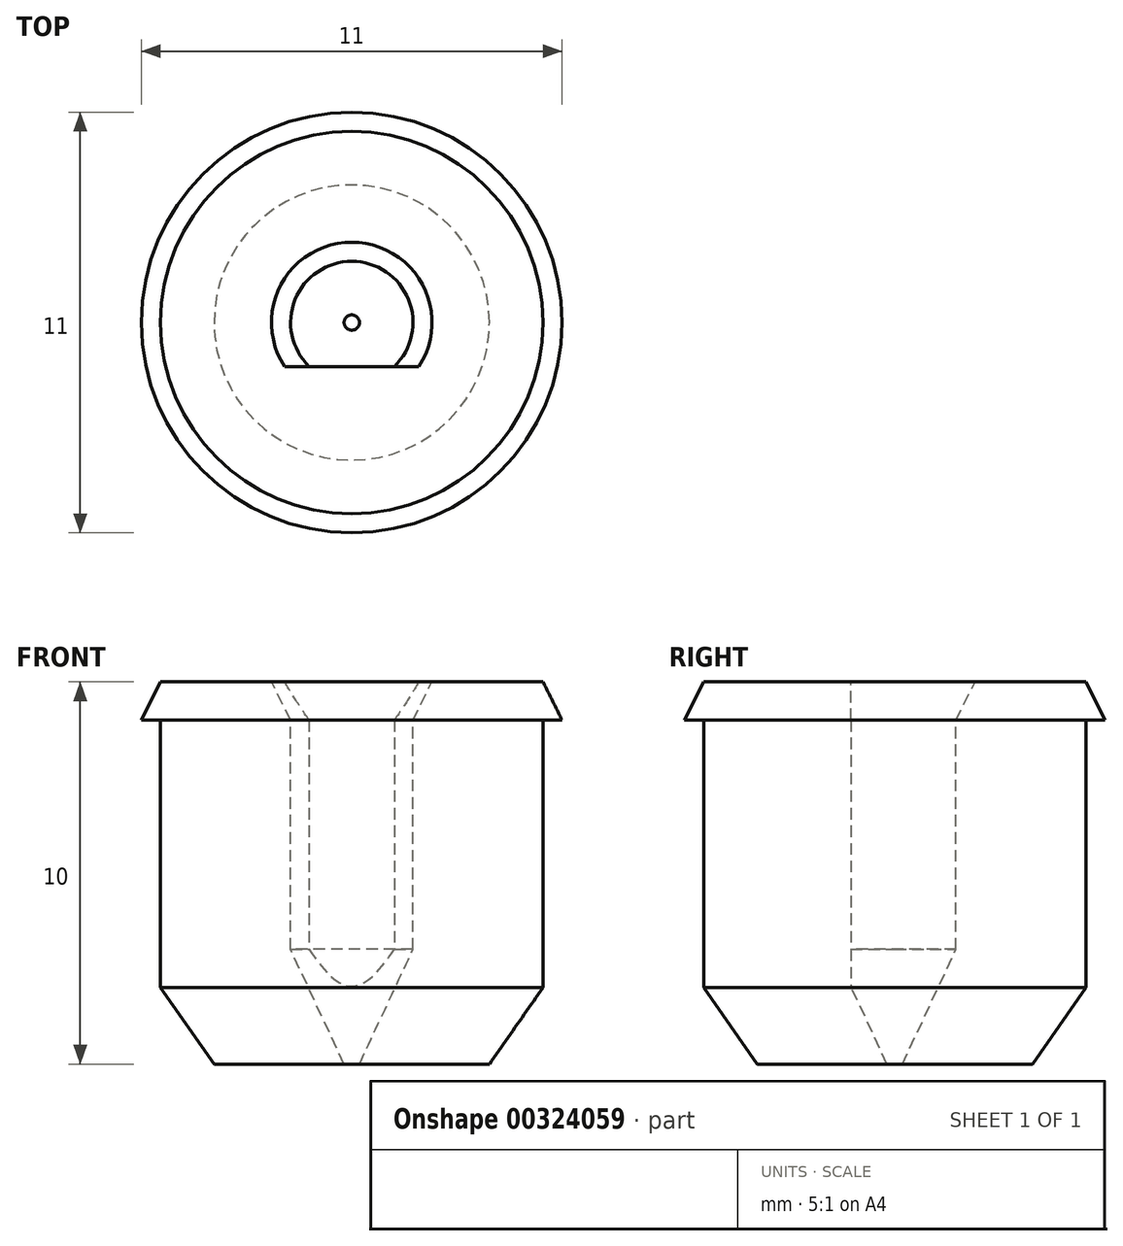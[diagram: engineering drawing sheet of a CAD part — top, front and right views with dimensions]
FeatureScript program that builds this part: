
annotation { "Feature Type Name" : "Feature", "Feature Type Description" : "" }
export const myFeature = defineFeature(function(context is Context, id is Id, definition is map)
    precondition{}
    {
        {
            var Q0;
            Q0=qCreatedBy(makeId("Front.planeOp"),FACE);
            var sketch = newSketch(context, id + "F0", { "sketchPlane" : qUnion([Q0])});
            skLineSegment(sketch, "E0", {"start": v(1.6, 10) * mm, "end": v(5.5, 10) * mm});
            skLineSegment(sketch, "E1", {"start": v(5.5, 10) * mm, "end": v(5.5, 9) * mm});
            skLineSegment(sketch, "E2", {"start": v(5.5, 9) * mm, "end": v(5, 9) * mm});
            skLineSegment(sketch, "E3", {"start": v(5, 9) * mm, "end": v(5, 2) * mm});
            skLineSegment(sketch, "E4", {"start": v(5, 2) * mm, "end": v(3.6, 0) * mm});
            skLineSegment(sketch, "E5", {"start": v(3.6, 0) * mm, "end": v(1.6, 0) * mm});
            skLineSegment(sketch, "E6", {"start": v(1.6, 0) * mm, "end": v(1.6, 10) * mm});
            skLineSegment(sketch, "E7", {"start": v(1.6, 3) * mm, "end": v(0.2, 0) * mm});
            skLineSegment(sketch, "E8", {"start": v(0, 10) * mm, "end": v(0, 0) * mm, "construction": true});
            skLineSegment(sketch, "E9", {"start": v(1.6, 0) * mm, "end": v(0.2, 0) * mm});
            skSolve(sketch);
        }
        {
            var Q0;
            Q0=makeQuery(id+"F0.imprint","IMPRINT",FACE,{"disambiguationData":[TD([[makeQuery(id+"F0.imprint","IMPRINT",EDGE,{"derivedFrom":sQuery(id+"F0.wireOp",EDGE,"E0")}),-1.0]])]});
            var Q1;
            {var subQ2=sQuery(id+"F0.wireOp",EDGE,"E7");Q1=makeQuery(id+"F0.imprint","IMPRINT",FACE,{"disambiguationData":[TD([[makeQuery(id+"F0.imprint","IMPRINT",EDGE,{"derivedFrom":subQ2}),1.0]])]});}
            var Q2;
            Q2=sQuery(id+"F0.wireOp",EDGE,"E8");
            revolve(context, id + "F1", {"entities" : qUnion([Q0, Q1]), "axis" : qUnion([Q2]), "revolveType" : RevolveType.FULL});
        }
        {
            var Q0;
            Q0=makeQuery(id+"F1.opRevolve","SWEPT_FACE",FACE,{"disambiguationData":[OSD([sQuery(id+"F0.wireOp",EDGE,"E5"),sQuery(id+"F0.wireOp",EDGE,"kTf56JAf-eDtF-ZYuP-kc0N-OWTcidlOXYet")])]});
            var sketch = newSketch(context, id + "F2", { "sketchPlane" : qUnion([Q0])});
            skCircle(sketch, "E10.0", {"center": v(0, 0) * mm, "radius": 1.6 * mm});
            skLineSegment(sketch, "E11", {"start": v(-1.11, 1.15) * mm, "end": v(1.11, 1.15) * mm});
            skSolve(sketch);
        }
        {
            var Q0;
            {var subQ0=sQuery(id+"F2.wireOp",EDGE,"E11");Q0=makeQuery(id+"F2.imprint","IMPRINT",FACE,{"disambiguationData":[TD([[makeQuery(id+"F2.imprint","IMPRINT",EDGE,{"derivedFrom":subQ0}),1.0]])]});}
            var Q1;
            {var subQ0=sQuery(id+"F2.wireOp",EDGE,"E11");var subQ1=makeQuery(id+"F1.opRevolve","SWEPT_EDGE",EDGE,{"disambiguationData":[OSD([sQuery(id+"F0.wireOp",EDGE,"E7"),sQuery(id+"F0.wireOp",EDGE,"kTf56JAf-eDtF-ZYuP-kc0N-OWTcidlOXYet")])]});var subQ2=makeQuery(id+"F2.imprint","INTERSECT",VERTEX,{"disambiguationData":[OD(0.0)],"derivedFrom":[subQ1,subQ0]});Q1=makeQuery(id+"F2.imprint","IMPRINT",FACE,{"disambiguationData":[TD([[makeQuery(id+"F2.imprint","IMPRINT",EDGE,{"disambiguationData":[TD([[subQ2,-1.0]])],"derivedFrom":subQ0}),1.0]])]});}
            var Q2;
            Q2=makeQuery(id+"F1.opRevolve","SWEPT_FACE",FACE,{"disambiguationData":[OSD([sQuery(id+"F0.wireOp",EDGE,"E0")])]});
            extrude(context, id + "F3", {"entities" : qUnion([Q0, Q1]), "operationType" : NewBodyOperationType.ADD, "endBound" : BoundingType.UP_TO_SURFACE, "oppositeDirection" : true, "endBoundEntityFace" : qUnion([Q2]), "depth" : 25 * mm});
        }
        {
            var Q0;
            Q0=makeQuery(id+"F3.opExtrude","TWEAK_EDGE",EDGE,{"derivedFrom":[makeQuery(id+"F1.opRevolve","SWEPT_FACE",FACE,{"disambiguationData":[OSD([sQuery(id+"F0.wireOp",EDGE,"E0")])]}),makeQuery(id+"F2.imprint","IMPRINT",EDGE,{"derivedFrom":sQuery(id+"F2.wireOp",EDGE,"E11")})]});
            var Q1;
            Q1=makeQuery(id+"F1.opRevolve","SWEPT_EDGE",EDGE,{"disambiguationData":[OSD([sQuery(id+"F0.wireOp",EDGE,"E0"),sQuery(id+"F0.wireOp",EDGE,"E6")])]});
            var Q2;
            Q2=makeQuery(id+"F1.opRevolve","SWEPT_EDGE",EDGE,{"disambiguationData":[OSD([sQuery(id+"F0.wireOp",EDGE,"E0"),sQuery(id+"F0.wireOp",EDGE,"E1")])]});
            chamfer(context, id + "F4", {"entities" : qUnion([Q0, Q1, Q2]), "chamferType" : ChamferType.TWO_OFFSETS, "width1" : .5 * mm, "oppositeDirection" : true, "width2" : 1 * mm, "tangentPropagation" : true});
        }
    });
